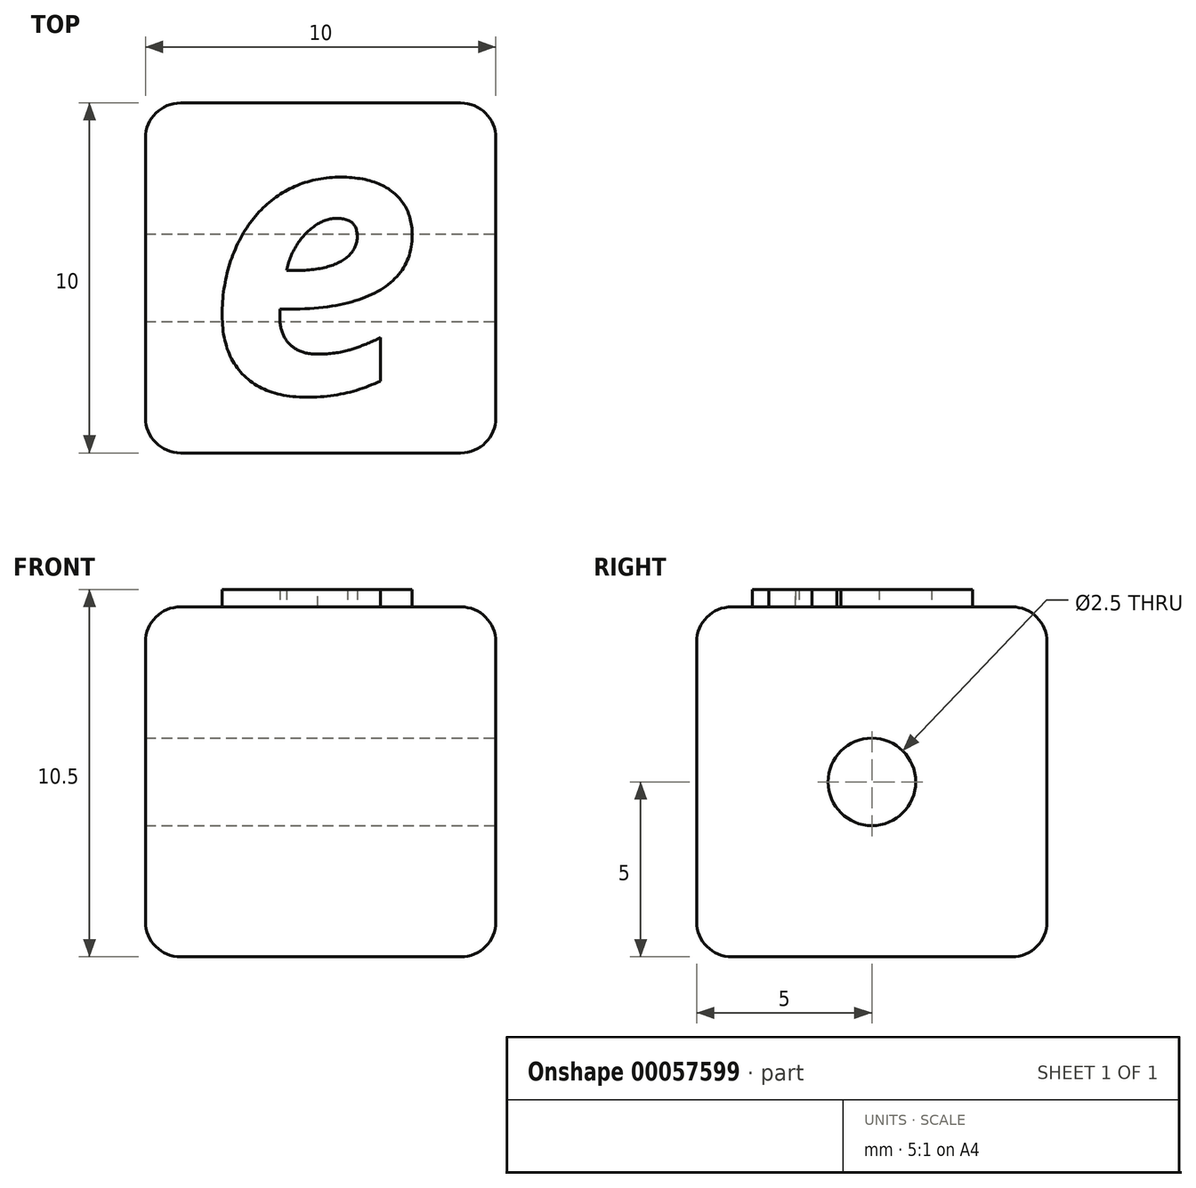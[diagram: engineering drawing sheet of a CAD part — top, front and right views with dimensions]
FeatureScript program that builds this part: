
annotation { "Feature Type Name" : "Feature", "Feature Type Description" : "" }
export const myFeature = defineFeature(function(context is Context, id is Id, definition is map)
    precondition{}
    {
        {
            var Q0;
            Q0=qCreatedBy(makeId("Top.planeOp"),FACE);
            var sketch = newSketch(context, id + "F0", { "sketchPlane" : qUnion([Q0])});
            skLineSegment(sketch, "E0.bottom", {"start": v(-5, 5) * mm, "end": v(5, 5) * mm});
            skLineSegment(sketch, "E0.top", {"start": v(-5, -5) * mm, "end": v(5, -5) * mm});
            skLineSegment(sketch, "E0.left", {"start": v(-5, 5) * mm, "end": v(-5, -5) * mm});
            skLineSegment(sketch, "E0.right", {"start": v(5, 5) * mm, "end": v(5, -5) * mm});
            skPoint(sketch, "E0.middle", {"position": v(0, 0) * mm});
            skSolve(sketch);
        }
        {
            var Q0;
            Q0=makeQuery(id+"F0.imprint","IMPRINT",FACE,{"disambiguationData":[TD([[makeQuery(id+"F0.imprint","IMPRINT",EDGE,{"derivedFrom":sQuery(id+"F0.wireOp",EDGE,"E0.bottom")}),-1.0]])]});
            extrude(context, id + "F1", {"entities" : qUnion([Q0]), "depth" : 10 * mm});
        }
        {
            var Q0;
            Q0=makeQuery(id+"F1.opExtrude","CAP_EDGE",EDGE,{"disambiguationData":[OSD([sQuery(id+"F0.wireOp",EDGE,"E0.left")])],"isStart":true});
            var Q1;
            Q1=makeQuery(id+"F1.opExtrude","CAP_EDGE",EDGE,{"disambiguationData":[OSD([sQuery(id+"F0.wireOp",EDGE,"E0.top")])],"isStart":true});
            var Q2;
            Q2=makeQuery(id+"F1.opExtrude","CAP_EDGE",EDGE,{"disambiguationData":[OSD([sQuery(id+"F0.wireOp",EDGE,"E0.right")])],"isStart":true});
            var Q3;
            Q3=makeQuery(id+"F1.opExtrude","CAP_EDGE",EDGE,{"disambiguationData":[OSD([sQuery(id+"F0.wireOp",EDGE,"E0.bottom")])],"isStart":true});
            var Q4;
            Q4=makeQuery(id+"F1.opExtrude","SWEPT_EDGE",EDGE,{"disambiguationData":[OSD([sQuery(id+"F0.wireOp",EDGE,"E0.top"),sQuery(id+"F0.wireOp",EDGE,"E0.left")])]});
            var Q5;
            Q5=makeQuery(id+"F1.opExtrude","SWEPT_EDGE",EDGE,{"disambiguationData":[OSD([sQuery(id+"F0.wireOp",EDGE,"E0.top"),sQuery(id+"F0.wireOp",EDGE,"E0.right")])]});
            var Q6;
            Q6=makeQuery(id+"F1.opExtrude","CAP_EDGE",EDGE,{"disambiguationData":[OSD([sQuery(id+"F0.wireOp",EDGE,"E0.top")])],"isStart":false});
            var Q7;
            Q7=makeQuery(id+"F1.opExtrude","CAP_EDGE",EDGE,{"disambiguationData":[OSD([sQuery(id+"F0.wireOp",EDGE,"E0.right")])],"isStart":false});
            var Q8;
            Q8=makeQuery(id+"F1.opExtrude","CAP_EDGE",EDGE,{"disambiguationData":[OSD([sQuery(id+"F0.wireOp",EDGE,"E0.left")])],"isStart":false});
            var Q9;
            Q9=makeQuery(id+"F1.opExtrude","CAP_EDGE",EDGE,{"disambiguationData":[OSD([sQuery(id+"F0.wireOp",EDGE,"E0.bottom")])],"isStart":false});
            var Q10;
            Q10=makeQuery(id+"F1.opExtrude","SWEPT_EDGE",EDGE,{"disambiguationData":[OSD([sQuery(id+"F0.wireOp",EDGE,"E0.bottom"),sQuery(id+"F0.wireOp",EDGE,"E0.right")])]});
            var Q11;
            Q11=makeQuery(id+"F1.opExtrude","SWEPT_EDGE",EDGE,{"disambiguationData":[OSD([sQuery(id+"F0.wireOp",EDGE,"E0.bottom"),sQuery(id+"F0.wireOp",EDGE,"E0.left")])]});
            fillet(context, id + "F2", {"entities" : qUnion([Q0, Q1, Q2, Q3, Q4, Q5, Q6, Q7, Q8, Q9, Q10, Q11]), "radius" : 1 * mm, "tangentPropagation" : true, "allowEdgeOverflow" : false});
        }
        {
            var Q0;
            Q0=makeQuery(id+"F1.opExtrude","CAP_FACE",FACE,{"disambiguationData":[OSD([sQuery(id+"F0.wireOp",EDGE,"E0.bottom"),sQuery(id+"F0.wireOp",EDGE,"E0.top"),sQuery(id+"F0.wireOp",EDGE,"E0.left"),sQuery(id+"F0.wireOp",EDGE,"E0.right")])],"isStart":false});
            var sketch = newSketch(context, id + "F3", { "sketchPlane" : qUnion([Q0])});
            skText(sketch, "E1", { "text": "e", "fontName": "OpenSans-BoldItalic.ttf"});
            const initialGuessF3  = {"E1": [-0.0033, -0.0033, 1, 0, 0.008]};
            skSetInitialGuess(sketch, initialGuessF3);
            skSolve(sketch);
        }
        {
            var Q0;
            Q0=makeQuery(id+"F3.imprint","IMPRINT",FACE,{"disambiguationData":[TD([[makeQuery(id+"F3.imprint","IMPRINT",EDGE,{"derivedFrom":sQuery(id+"F3.wireOp",EDGE,"E1.sketch_text.stroke-0")}),-1.0]])]});
            extrude(context, id + "F4", {"entities" : qUnion([Q0]), "operationType" : NewBodyOperationType.ADD, "depth" : .5 * mm});
        }
        {
            var Q0;
            Q0=makeQuery(id+"F1.opExtrude","SWEPT_FACE",FACE,{"disambiguationData":[OSD([sQuery(id+"F0.wireOp",EDGE,"E0.right")])]});
            var sketch = newSketch(context, id + "F5", { "sketchPlane" : qUnion([Q0])});
            skCircle(sketch, "E2", {"center": v(0, 5) * mm, "radius": 1.25 * mm});
            skPoint(sketch, "E2.centerSnap0", {"position": v(4, 5) * mm});
            skPoint(sketch, "E2.centerSnap1", {"position": v(0, 1) * mm});
            skSolve(sketch);
        }
        {
            var Q0;
            Q0=makeQuery(id+"F5.imprint","IMPRINT",FACE,{"disambiguationData":[TD([[makeQuery(id+"F5.imprint","IMPRINT",EDGE,{"derivedFrom":sQuery(id+"F5.wireOp",EDGE,"E2")}),1.0]])]});
            extrude(context, id + "F6", {"entities" : qUnion([Q0]), "operationType" : NewBodyOperationType.REMOVE, "oppositeDirection" : true, "depth" : 25 * mm});
        }
    });
